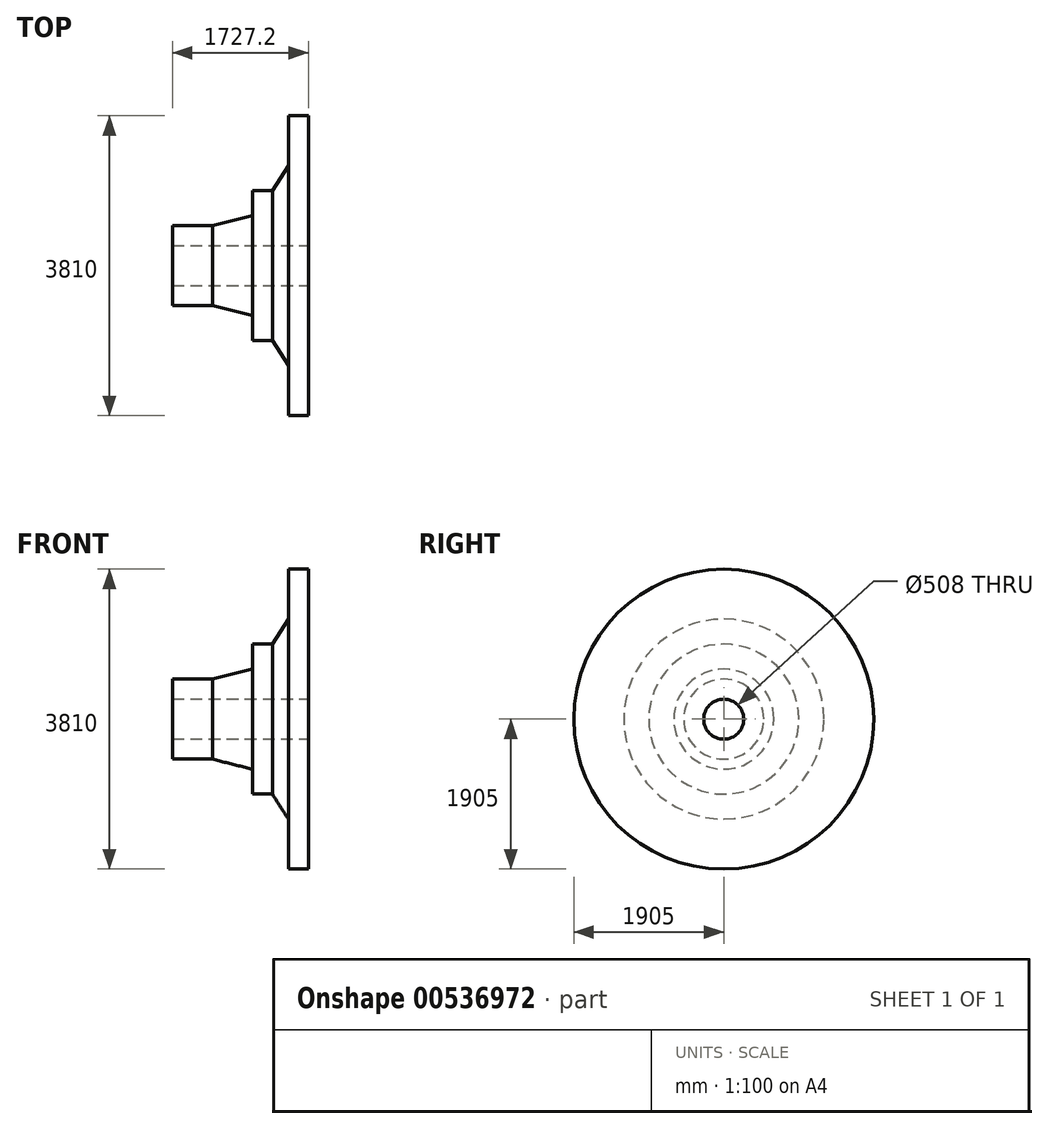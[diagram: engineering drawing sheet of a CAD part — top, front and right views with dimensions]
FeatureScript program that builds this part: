
annotation { "Feature Type Name" : "Feature", "Feature Type Description" : "" }
export const myFeature = defineFeature(function(context is Context, id is Id, definition is map)
    precondition{}
    {
        {
            var Q0;
            Q0=qCreatedBy(makeId("Front.planeOp"),FACE);
            var sketch = newSketch(context, id + "F0", { "sketchPlane" : qUnion([Q0])});
            skLineSegment(sketch, "E0", {"start": v(888.42, -666.62) * mm, "end": v(-838.78, -666.62) * mm});
            skLineSegment(sketch, "E1", {"start": v(-838.78, -666.62) * mm, "end": v(-838.78, -412.62) * mm});
            skLineSegment(sketch, "E2", {"start": v(-838.78, -412.62) * mm, "end": v(-330.78, -412.62) * mm});
            skLineSegment(sketch, "E3", {"start": v(-330.78, -412.62) * mm, "end": v(177.22, -285.62) * mm});
            skLineSegment(sketch, "E4", {"start": v(431.22, 31.88) * mm, "end": v(634.42, 349.38) * mm});
            skLineSegment(sketch, "E5", {"start": v(634.42, 349.38) * mm, "end": v(634.42, 984.38) * mm});
            skLineSegment(sketch, "E6", {"start": v(634.42, 984.38) * mm, "end": v(888.42, 984.38) * mm});
            skLineSegment(sketch, "E7", {"start": v(888.42, 984.38) * mm, "end": v(888.42, -666.62) * mm});
            skLineSegment(sketch, "E8", {"start": v(177.22, -285.62) * mm, "end": v(177.22, 31.88) * mm});
            skLineSegment(sketch, "E9", {"start": v(177.22, 31.88) * mm, "end": v(431.22, 31.88) * mm});
            skLineSegment(sketch, "E10", {"start": v(959.7, -920.62) * mm, "end": v(-1665.43, -920.62) * mm});
            skSolve(sketch);
        }
        {
            var Q0;
            Q0 = qSketchRegion(id + "F0", true);
            var Q1;
            Q1=sQuery(id+"F0.wireOp",EDGE,"E10");
            revolve(context, id + "F1", {"entities" : qUnion([Q0]), "axis" : qUnion([Q1]), "revolveType" : RevolveType.FULL});
        }
    });
